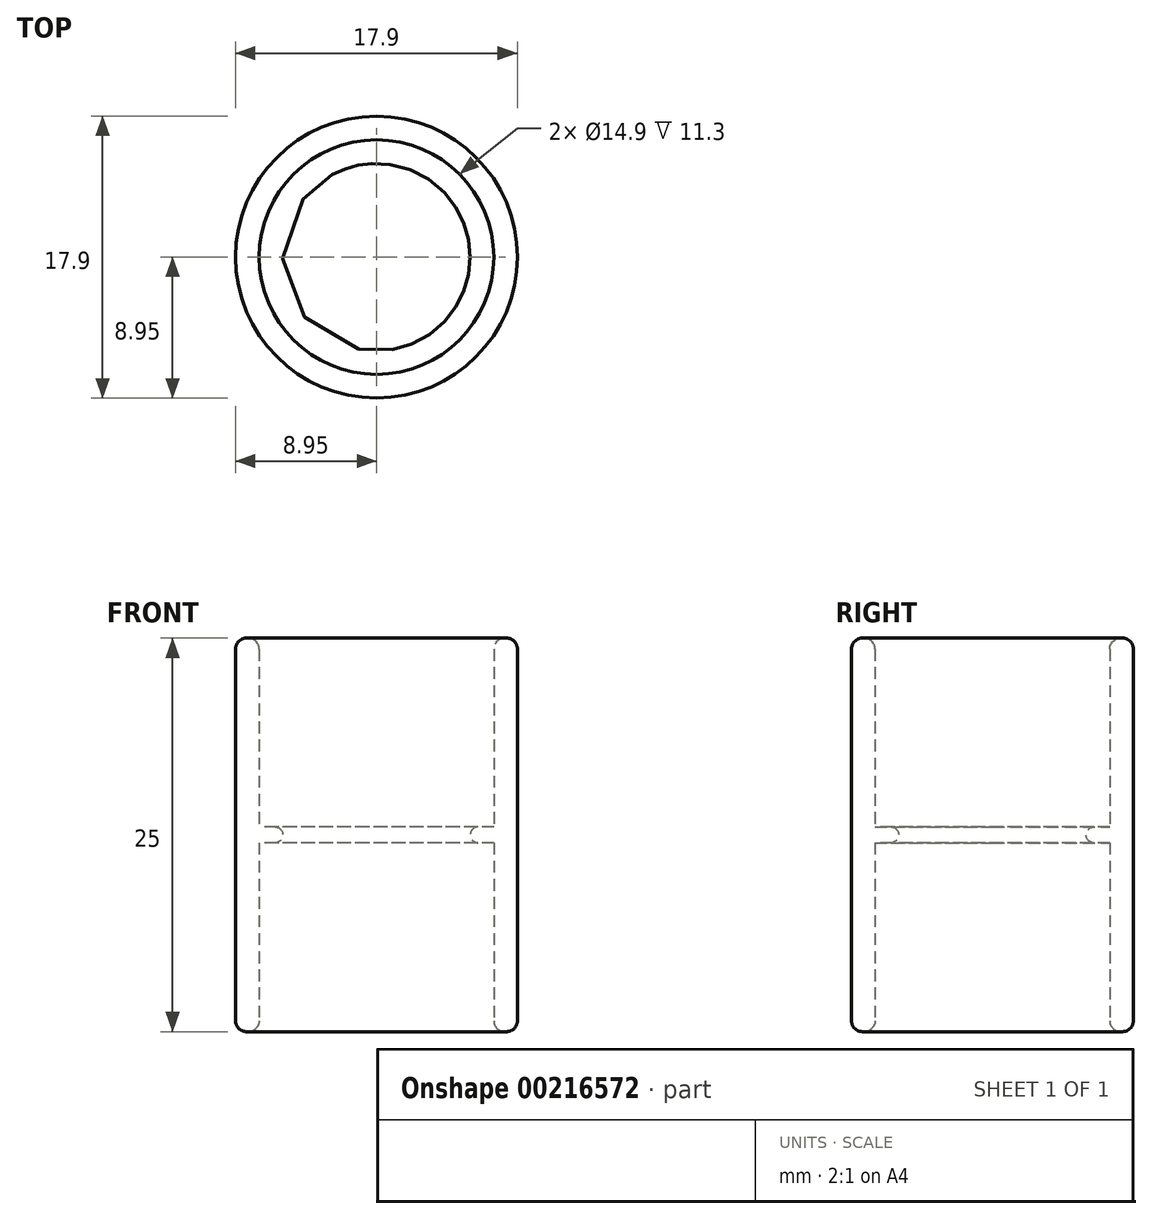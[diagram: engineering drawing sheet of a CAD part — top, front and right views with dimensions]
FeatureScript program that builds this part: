
annotation { "Feature Type Name" : "Feature", "Feature Type Description" : "" }
export const myFeature = defineFeature(function(context is Context, id is Id, definition is map)
    precondition{}
    {
        {
            var Q0;
            Q0=qCreatedBy(makeId("Top.planeOp"),FACE);
            var sketch = newSketch(context, id + "F0", { "sketchPlane" : qUnion([Q0])});
            skCircle(sketch, "E0", {"center": v(0, 0) * mm, "radius": 7.45 * mm});
            skCircle(sketch, "E1.0", {"center": v(0, 0) * mm, "radius": 8.95 * mm});
            skCircle(sketch, "E2.0", {"center": v(0, 0) * mm, "radius": 5.95 * mm});
            skSolve(sketch);
        }
        {
            var Q0;
            Q0=makeQuery(id+"F0.imprint","IMPRINT",FACE,{"disambiguationData":[TD([[makeQuery(id+"F0.imprint","IMPRINT",EDGE,{"derivedFrom":sQuery(id+"F0.wireOp",EDGE,"E0")}),-1.0]])]});
            extrude(context, id + "F1", {"entities" : qUnion([Q0]), "depth" : 25 * mm});
        }
        {
            var Q0;
            Q0=makeQuery(id+"F0.imprint","IMPRINT",FACE,{"disambiguationData":[TD([[makeQuery(id+"F0.imprint","IMPRINT",EDGE,{"derivedFrom":sQuery(id+"F0.wireOp",EDGE,"E0")}),1.0]])]});
            extrude(context, id + "F2", {"entities" : qUnion([Q0]), "operationType" : NewBodyOperationType.ADD, "depth" : 13 * mm, "hasSecondDirection" : true, "secondDirectionOppositeDirection" : false, "secondDirectionDepth" : 12 * mm});
        }
        {
            var Q0;
            Q0=makeQuery(id+"F1.opExtrude","CAP_FACE",FACE,{"disambiguationData":[OSD([sQuery(id+"F0.wireOp",EDGE,"E0"),sQuery(id+"F0.wireOp",EDGE,"E1.0")])],"isStart":false});
            var Q1;
            Q1=makeQuery(id+"F1.opExtrude","CAP_FACE",FACE,{"disambiguationData":[OSD([sQuery(id+"F0.wireOp",EDGE,"E0"),sQuery(id+"F0.wireOp",EDGE,"E1.0")])],"isStart":true});
            fillet(context, id + "F3", {"entities" : qUnion([Q0, Q1]), "radius" : 0.7 * mm, "tangentPropagation" : true, "allowEdgeOverflow" : false});
        }
        {
            var Q0;
            Q0=makeQuery(id+"F2.opExtrude","SWEPT_FACE",FACE,{"disambiguationData":[OSD([sQuery(id+"F0.wireOp",EDGE,"E2.0")])]});
            fillet(context, id + "F4", {"entities" : qUnion([Q0]), "radius" : 0.5 * mm, "tangentPropagation" : true, "allowEdgeOverflow" : false});
        }
    });
